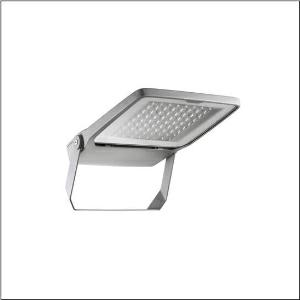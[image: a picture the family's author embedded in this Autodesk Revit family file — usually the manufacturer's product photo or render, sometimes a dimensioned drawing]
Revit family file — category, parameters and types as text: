
# Revit family: floodlight_fl_20_mini___pl43_5xa7672c1a1ac_9437
name_source: partatom
category: Lighting Fixtures
units: mm (PartAtom-declared; Revit-internal decimal feet)

## family parameters
Cut with Voids When Loaded = No
Host = Face
Light Source = No
Part Type = Normal
Room Calculation Point = No
Round Connector Dimension = Use Diameter
Shared = No

## types (1)
- --- (1 x LED 3000K / CRI = 80 (unbekannt), 10230 lm, 3000K)
    Apparent Load = 96 VA
    CIE Flux Codes = 32 74 99 100 100
    Color Rendering = 80
    Color Temperature = 3000K
    Default Elevation = 1800 mm
    Description = Floodlight FL 20 mini, floodlight, primary light control with lens, of plastic, primary optical cover: protective disc, of toughened safety glass, transparent, light distribution: PL43, light emission: direct distribution, primary light characteristic: asymmetric, installation type: surface-mounted, LED, High Power LED, rated luminous flux: 10.230lm, luminous efficacy: 107lm/W, light colour: 830, colour temperature: 3000K, control gear: ECG Plus, control: flexible luminous flux parameterisation, time-dependent luminous flux control, digital communication interface, power reduction, overheat protection, electronic power reduction, with terminal, 5-pole, max. 2.5mm², mains connection: 220..240V, AC, 50/60Hz, rated input power: 96W, LED unit, of diecast aluminium, powder-coated, Siteco® metallic grey (DB 702S), corrosivity category C5 mid according to DIN EN ISO 12944, incl. 1x M20 cable gland for cable Ø 6.5..12mm, length: 446mm, width: 355mm, height: 62mm, housing frame, of diecast aluminium, powder-coated, Siteco® metallic grey (DB 702S), mounting bracket, of steel, powder-coated, Siteco® metallic grey (DB 702S), DALI, protection rating (complete): IP66, insulation class (complete): insulation class II (safety insulation), certification: CE, ENEC, VDE, protection symbol: D, permissible operating ambient temperature: -40..+40°C, permissible operating ambient temperature for outdoor applications: -40..+50°C, standard: DIN EN 12944, packaging unit: 1 piece

Light Distribution: PL43
    Height = 62 mm  [stored 0.203412 ft]
    Lamp = 1 x LED 3000K / CRI >= 80 (unbekannt)
    Lamp Light Flux = 10230 lm
    Lamp count = 1
    Length = 467 mm
    Luminous efficacy = 107 lm/W
    Manufacturer = Siteco
    ModVariant = No
    Model = 5XA7672C1A1AC
    Mounting Place = Wall
    Mounting Type = Surface mounted
    Number of Poles = 1
    OnlyDefault = Yes
    Power Factor = 1
    Product Name = Floodlight FL 20 mini | PL43
    Product group = floodlight | wall mounted
    ProductGroupID = 2001
    Protection Class = Protection class II
    Protection Degree = IP 66
    RLX_Detail_Level = 1
    RLX_Emergency_Light_Flux = 0 lm
    RLX_Emergency_Type = 0
    RLX_Emergency_Type_DB = No
    RlxData = <blob elided: 74037 chars, md5=78686e17>
    Socket = socket
    Standby Power = 0 W
    System Light Flux = 10230 lm
    System Power = 96 W
    Type Comments = factory setting: luminous flux: 100 % | dim-lin: 254 | 500 mA
    Type Image = l_1005948.jpg
    URL = http://relux.com
    VarID = @adj_164357
    Voltage = 0 V
    Weight = 0.00 kg
    Width = 335 mm

note: [stored X ft] marks values corroborated as IEEE doubles in the binary element streams (Revit-internal decimal feet)

## geometry (parser evidence)
native form markers: Blend x4, Sweep x14
no freeform markers — native parametric forms only
